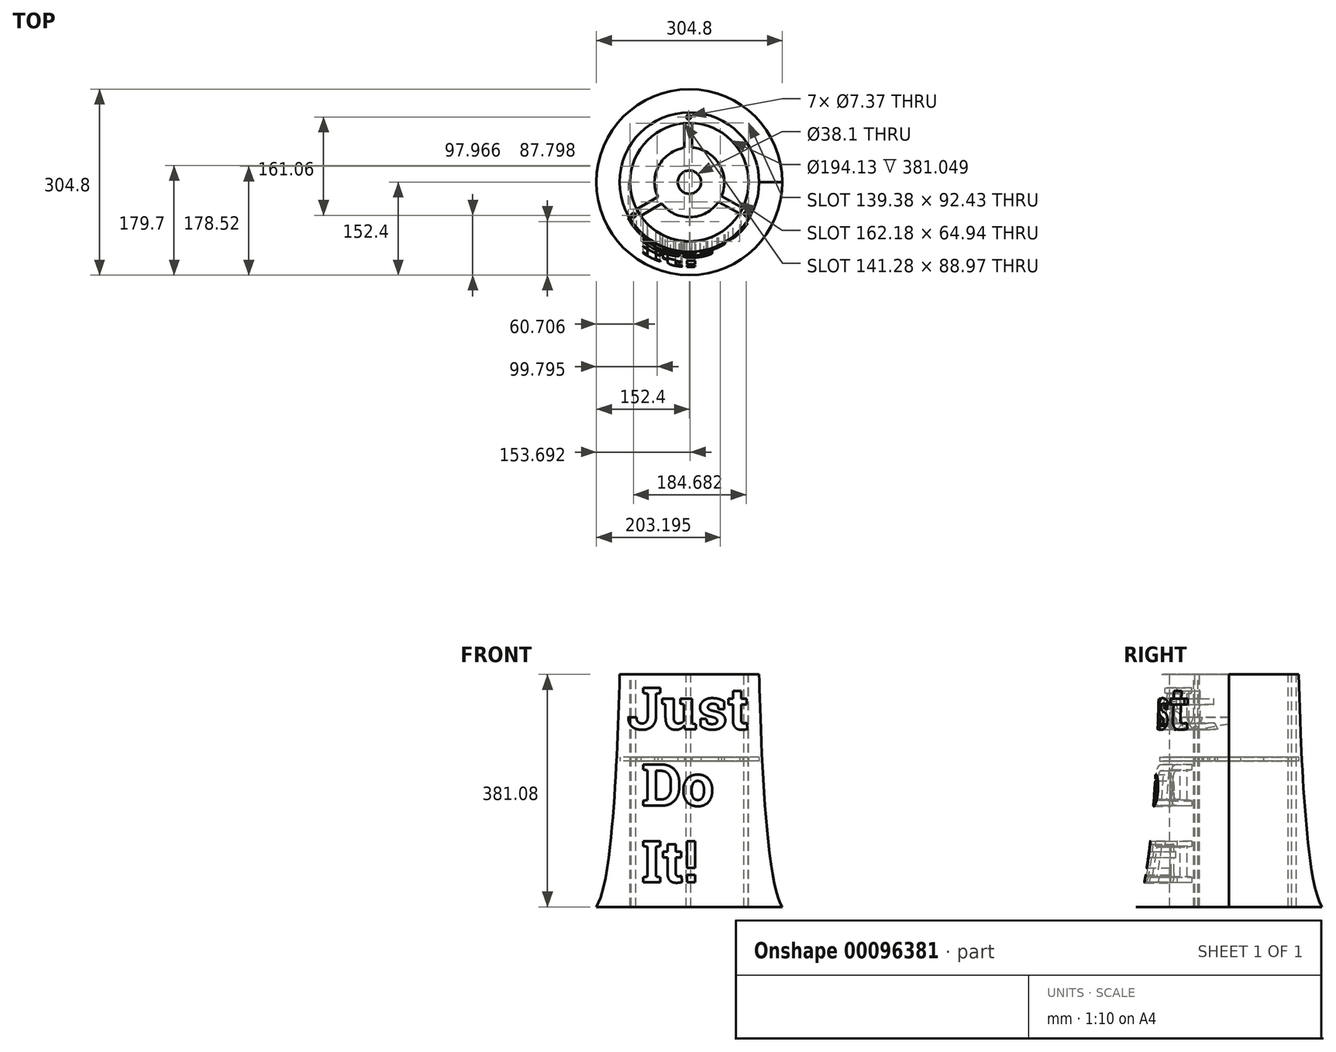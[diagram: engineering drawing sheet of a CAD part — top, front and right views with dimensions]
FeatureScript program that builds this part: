
annotation { "Feature Type Name" : "Feature", "Feature Type Description" : "" }
export const myFeature = defineFeature(function(context is Context, id is Id, definition is map)
    precondition{}
    {
        {
            var Q0;
            Q0=qCreatedBy(makeId("Front.planeOp"),FACE);
            var sketch = newSketch(context, id + "F0", { "sketchPlane" : qUnion([Q0])});
            skPoint(sketch, "E0", {"position": v(114.3, 294.45) * mm});
            skFitSpline(sketch, "E1", {"points": [v(114.3, 294.45) * mm, v(152.4, -86.63) * mm], "startDerivative": vector(6.03, -229.97) * mm, "endDerivative": vector(87.35, -124.89) * mm});
            skLineSegment(sketch, "E2", {"start": v(0, 294.45) * mm, "end": v(0, -86.55) * mm});
            skLineSegment(sketch, "E3", {"start": v(0, 294.45) * mm, "end": v(114.3, 294.45) * mm});
            skLineSegment(sketch, "E4", {"start": v(0, -86.55) * mm, "end": v(152.4, -86.63) * mm});
            skSolve(sketch);
        }
        {
            var Q0;
            Q0=makeQuery(id+"F0.imprint","IMPRINT",FACE,{"disambiguationData":[TD([[makeQuery(id+"F0.imprint","IMPRINT",EDGE,{"derivedFrom":sQuery(id+"F0.wireOp",EDGE,"E1")}),-1.0]])]});
            var Q1;
            Q1=sQuery(id+"F0.wireOp",EDGE,"E2");
            revolve(context, id + "F1", {"entities" : qUnion([Q0]), "axis" : qUnion([Q1]), "revolveType" : RevolveType.FULL});
        }
        {
            var Q0;
            Q0=makeQuery(id+"F1.opRevolve","SWEPT_FACE",FACE,{"disambiguationData":[OSD([sQuery(id+"F0.wireOp",EDGE,"E3")])]});
            var sketch = newSketch(context, id + "F2", { "sketchPlane" : qUnion([Q0])});
            skCircle(sketch, "E5", {"center": v(0, 0) * mm, "radius": 97.07 * mm});
            skSolve(sketch);
        }
        {
            var Q0;
            Q0 = qSketchRegion(id + "F2", true);
            extrude(context, id + "F3", {"entities" : qUnion([Q0]), "operationType" : NewBodyOperationType.REMOVE, "oppositeDirection" : true, "depth" : 420.5 * mm});
        }
        {
            var Q0;
            Q0=makeQuery(id+"F1.opRevolve","SWEPT_FACE",FACE,{"disambiguationData":[OSD([sQuery(id+"F0.wireOp",EDGE,"E3")])]});
            var sketch = newSketch(context, id + "F4", { "sketchPlane" : qUnion([Q0])});
            skCircle(sketch, "E6", {"center": v(-1.3, 106.63) * mm, "radius": 3.68 * mm});
            skCircle(sketch, "E7.1.0", {"center": v(-91.7, -54.43) * mm, "radius": 3.68 * mm});
            skCircle(sketch, "E7.2.0", {"center": v(92.99, -52.2) * mm, "radius": 3.68 * mm});
            skPoint(sketch, "E7.center", {"position": v(0, 0) * mm});
            skSolve(sketch);
        }
        {
            var Q0;
            Q0=qCreatedBy(makeId("Front.planeOp"),FACE);
            var sketch = newSketch(context, id + "F5", { "sketchPlane" : qUnion([Q0])});
            skText(sketch, "E8", { "text": " Just\n  Do\n  It!", "fontName": "RobotoSlab-Bold.ttf"});
            const initialGuessF5  = {"E8": [-0.1249, 0.2047, 1, 0, 0.06844]};
            skSetInitialGuess(sketch, initialGuessF5);
            skSolve(sketch);
        }
        {
            var Q0;
            Q0 = qSketchRegion(id + "F5", true);
            extrude(context, id + "F6", {"entities" : qUnion([Q0]), "operationType" : NewBodyOperationType.REMOVE, "depth" : 216.67 * mm});
        }
        {
            var Q0;
            Q0=qCreatedBy(makeId("Top.planeOp"),FACE);
            cPlane(context, id + "F7", {"entities" : qUnion([Q0]), "cplaneType" : CPlaneType.OFFSET, "offset" : 152.4 * mm, "width" : 152.4 * mm, "height" : 152.4 * mm});
        }
        {
            var Q0;
            Q0=qCreatedBy(id+"F7.planeOp",FACE);
            var sketch = newSketch(context, id + "F8", { "sketchPlane" : qUnion([Q0])});
            skCircle(sketch, "E9", {"center": v(0, 0) * mm, "radius": 97.1 * mm});
            skCircle(sketch, "E10", {"center": v(0, 0) * mm, "radius": 113.86 * mm});
            skCircle(sketch, "E11", {"center": v(0.07, -0.32) * mm, "radius": 57.15 * mm});
            skLineSegment(sketch, "E12", {"start": v(-8.12, 96.76) * mm, "end": v(-8.12, 56.24) * mm});
            skLineSegment(sketch, "E13", {"start": v(4.58, 96.99) * mm, "end": v(4.58, 56.66) * mm});
            skLineSegment(sketch, "E14", {"start": v(-86.3, -44.52) * mm, "end": v(-51.77, -24.37) * mm});
            skLineSegment(sketch, "E15", {"start": v(-79.8, -55.32) * mm, "end": v(-45.45, -34.87) * mm});
            skLineSegment(sketch, "E16", {"start": v(47.54, -32.13) * mm, "end": v(82.38, -51.4) * mm});
            skLineSegment(sketch, "E17", {"start": v(52.62, -22.79) * mm, "end": v(87.36, -42.4) * mm});
            skSolve(sketch);
        }
        {
            var Q0;
            Q0 = qSketchRegion(id + "F8", true);
            var Q1;
            {var subQ0=sQuery(id+"F8.wireOp",EDGE,"E11");var subQ4=makeQuery(id+"F8.imprint","INTERSECT",VERTEX,{"derivedFrom":[subQ0,sQuery(id+"F8.wireOp",EDGE,"E12")]});Q1=makeQuery(id+"F8.imprint","IMPRINT",FACE,{"disambiguationData":[TD([[makeQuery(id+"F8.imprint","IMPRINT",EDGE,{"disambiguationData":[TD([[subQ4,1.0]])],"derivedFrom":subQ0}),1.0]])]});}
            var Q2;
            {var subQ0=sQuery(id+"F8.wireOp",EDGE,"E14");Q2=makeQuery(id+"F8.imprint","IMPRINT",FACE,{"disambiguationData":[TD([[makeQuery(id+"F8.imprint","IMPRINT",EDGE,{"derivedFrom":subQ0}),-1.0]])]});}
            var Q3;
            {var subQ0=sQuery(id+"F8.wireOp",EDGE,"E12");Q3=makeQuery(id+"F8.imprint","IMPRINT",FACE,{"disambiguationData":[TD([[makeQuery(id+"F8.imprint","IMPRINT",EDGE,{"derivedFrom":subQ0}),1.0]])]});}
            var Q4;
            {var subQ0=sQuery(id+"F8.wireOp",EDGE,"E16");Q4=makeQuery(id+"F8.imprint","IMPRINT",FACE,{"disambiguationData":[TD([[makeQuery(id+"F8.imprint","IMPRINT",EDGE,{"derivedFrom":subQ0}),1.0]])]});}
            extrude(context, id + "F9", {"entities" : qUnion([Q0, Q1, Q2, Q3, Q4]), "depth" : 6.35 * mm});
        }
        {
            var Q0;
            Q0=makeQuery(id+"F4.imprint","IMPRINT",FACE,{"disambiguationData":[TD([[makeQuery(id+"F4.imprint","IMPRINT",EDGE,{"derivedFrom":sQuery(id+"F4.wireOp",EDGE,"E7.1.0")}),1.0]])]});
            var Q1;
            Q1=makeQuery(id+"F4.imprint","IMPRINT",FACE,{"disambiguationData":[TD([[makeQuery(id+"F4.imprint","IMPRINT",EDGE,{"derivedFrom":sQuery(id+"F4.wireOp",EDGE,"E7.2.0")}),1.0]])]});
            var Q2;
            Q2=makeQuery(id+"F4.imprint","IMPRINT",FACE,{"disambiguationData":[TD([[makeQuery(id+"F4.imprint","IMPRINT",EDGE,{"derivedFrom":sQuery(id+"F4.wireOp",EDGE,"E6")}),1.0]])]});
            extrude(context, id + "F10", {"entities" : qUnion([Q0, Q1, Q2]), "operationType" : NewBodyOperationType.REMOVE, "oppositeDirection" : true, "depth" : 647 * mm});
        }
        {
            var Q0;
            Q0=qCreatedBy(makeId("Top.planeOp"),FACE);
            var sketch = newSketch(context, id + "F11", { "sketchPlane" : qUnion([Q0])});
            skCircle(sketch, "E18", {"center": v(0, 0) * mm, "radius": 19.05 * mm});
            skSolve(sketch);
        }
        {
            var Q0;
            Q0 = qSketchRegion(id + "F11", true);
            extrude(context, id + "F12", {"entities" : qUnion([Q0]), "operationType" : NewBodyOperationType.REMOVE, "depth" : 471.66 * mm});
        }
    });
